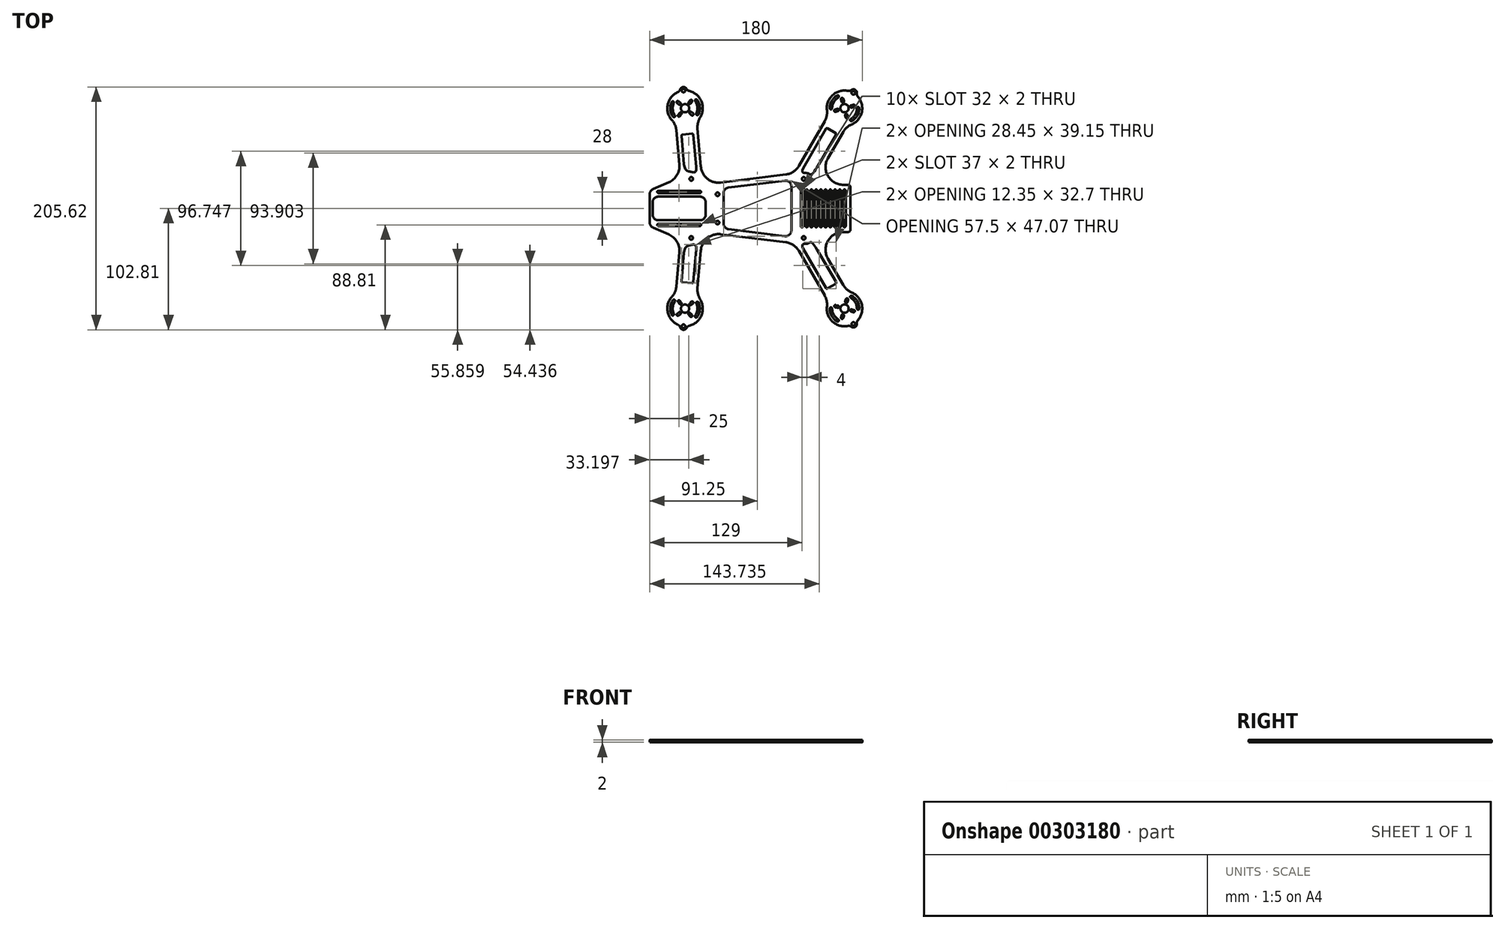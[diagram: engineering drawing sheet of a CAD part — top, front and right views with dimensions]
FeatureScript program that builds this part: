
annotation { "Feature Type Name" : "Feature", "Feature Type Description" : "" }
export const myFeature = defineFeature(function(context is Context, id is Id, definition is map)
    precondition{}
    {
        {
            var Q0;
            Q0=qCreatedBy(makeId("Top.planeOp"),FACE);
            var sketch = newSketch(context, id + "F0", { "sketchPlane" : qUnion([Q0])});
            skLineSegment(sketch, "E0", {"start": v(-85, 0) * mm, "end": v(85, 0) * mm, "construction": true});
            skLineSegment(sketch, "E1", {"start": v(-47.57, 0) * mm, "end": v(-55, -84.87) * mm, "construction": true});
            skLineSegment(sketch, "E2", {"start": v(31, 0) * mm, "end": v(80, -84.87) * mm, "construction": true});
            skArc(sketch, "E3", {"start": v(-66.17, -74.86) * mm, "mid": v(-69.65, -88.1) * mm, "end": v(-60.9, -98.66) * mm});
            skArc(sketch, "E4", {"start": v(65.1, -83.08) * mm, "mid": v(69.86, -95.92) * mm, "end": v(83.07, -99.55) * mm});
            skCircle(sketch, "E5", {"center": v(-55, -84.87) * mm, "radius": 3.5 * mm});
            skCircle(sketch, "E6", {"center": v(-55, -84.87) * mm, "radius": 6 * mm, "construction": true});
            skCircle(sketch, "E7", {"center": v(-55, -84.87) * mm, "radius": 8 * mm, "construction": true});
            skCircle(sketch, "E8", {"center": v(80, -84.87) * mm, "radius": 6 * mm, "construction": true});
            skCircle(sketch, "E9", {"center": v(80, -84.87) * mm, "radius": 8 * mm, "construction": true});
            skCircle(sketch, "E10", {"center": v(80, -84.87) * mm, "radius": 3.5 * mm});
            skLineSegment(sketch, "E11", {"start": v(-55, -84.87) * mm, "end": v(-58.86, -80.27) * mm, "construction": true});
            skLineSegment(sketch, "E12", {"start": v(80, -84.87) * mm, "end": v(81.55, -79.07) * mm, "construction": true});
            skLineSegment(sketch, "E13", {"start": v(-60.14, -78.74) * mm, "end": v(-64.05, -74.08) * mm, "construction": true});
            skLineSegment(sketch, "E14", {"start": v(-58.86, -80.27) * mm, "end": v(-60.14, -78.74) * mm, "construction": true});
            skArc(sketch, "E15.0.startCap", {"start": v(-58.1, -79.63) * mm, "mid": v(-58.21, -81.04) * mm, "end": v(-59.62, -80.92) * mm});
            skArc(sketch, "E15.0.endCap", {"start": v(-60.9, -79.38) * mm, "mid": v(-60.79, -77.98) * mm, "end": v(-59.38, -78.1) * mm});
            skLineSegment(sketch, "E15.0.left", {"start": v(-59.62, -80.92) * mm, "end": v(-60.9, -79.38) * mm});
            skLineSegment(sketch, "E15.0.right", {"start": v(-58.1, -79.63) * mm, "end": v(-59.38, -78.1) * mm});
            skArc(sketch, "E16.1.0", {"start": v(-60.49, -90.78) * mm, "mid": v(-61.9, -90.66) * mm, "end": v(-61.77, -89.25) * mm});
            skLineSegment(sketch, "E16.1.1", {"start": v(-60.24, -87.96) * mm, "end": v(-61.77, -89.25) * mm});
            skArc(sketch, "E16.1.2", {"start": v(-60.24, -87.96) * mm, "mid": v(-58.83, -88.08) * mm, "end": v(-58.95, -89.5) * mm});
            skLineSegment(sketch, "E16.1.3", {"start": v(-58.95, -89.5) * mm, "end": v(-60.49, -90.78) * mm});
            skArc(sketch, "E16.2.0", {"start": v(-49.1, -90.36) * mm, "mid": v(-49.21, -91.76) * mm, "end": v(-50.62, -91.64) * mm});
            skLineSegment(sketch, "E16.2.1", {"start": v(-51.9, -90.1) * mm, "end": v(-50.62, -91.64) * mm});
            skArc(sketch, "E16.2.2", {"start": v(-51.9, -90.1) * mm, "mid": v(-51.79, -88.7) * mm, "end": v(-50.38, -88.82) * mm});
            skLineSegment(sketch, "E16.2.3", {"start": v(-50.38, -88.82) * mm, "end": v(-49.1, -90.36) * mm});
            skArc(sketch, "E16.3.0", {"start": v(-49.51, -78.96) * mm, "mid": v(-48.1, -79.09) * mm, "end": v(-48.23, -80.5) * mm});
            skLineSegment(sketch, "E16.3.1", {"start": v(-49.76, -81.78) * mm, "end": v(-48.23, -80.5) * mm});
            skArc(sketch, "E16.3.2", {"start": v(-49.76, -81.78) * mm, "mid": v(-51.17, -81.66) * mm, "end": v(-51.05, -80.25) * mm});
            skLineSegment(sketch, "E16.3.3", {"start": v(-51.05, -80.25) * mm, "end": v(-49.51, -78.96) * mm});
            skCircle(sketch, "E17", {"center": v(-55, -84.87) * mm, "radius": 63.5 * mm, "construction": true});
            skCircle(sketch, "E18", {"center": v(80, -84.87) * mm, "radius": 63.5 * mm, "construction": true});
            skLineSegment(sketch, "E19", {"start": v(81.55, -79.07) * mm, "end": v(82.07, -77.14) * mm, "construction": true});
            skLineSegment(sketch, "E20", {"start": v(82.07, -77.14) * mm, "end": v(83.42, -72.1) * mm, "construction": true});
            skArc(sketch, "E21.0.startCap", {"start": v(82.52, -79.33) * mm, "mid": v(81.3, -80.04) * mm, "end": v(80.59, -78.82) * mm});
            skArc(sketch, "E21.0.endCap", {"start": v(81.1, -76.88) * mm, "mid": v(82.33, -76.18) * mm, "end": v(83.04, -77.4) * mm});
            skLineSegment(sketch, "E21.0.left", {"start": v(80.59, -78.82) * mm, "end": v(81.1, -76.88) * mm});
            skLineSegment(sketch, "E21.0.right", {"start": v(82.52, -79.33) * mm, "end": v(83.04, -77.4) * mm});
            skArc(sketch, "E22.1.0", {"start": v(72.01, -83.77) * mm, "mid": v(71.3, -82.54) * mm, "end": v(72.53, -81.83) * mm});
            skLineSegment(sketch, "E22.1.1", {"start": v(74.46, -82.35) * mm, "end": v(72.53, -81.83) * mm});
            skArc(sketch, "E22.1.2", {"start": v(74.46, -82.35) * mm, "mid": v(75.17, -83.58) * mm, "end": v(73.95, -84.28) * mm});
            skLineSegment(sketch, "E22.1.3", {"start": v(73.95, -84.28) * mm, "end": v(72.01, -83.77) * mm});
            skArc(sketch, "E22.2.0", {"start": v(78.9, -92.86) * mm, "mid": v(77.67, -93.56) * mm, "end": v(76.96, -92.34) * mm});
            skLineSegment(sketch, "E22.2.1", {"start": v(77.48, -90.4) * mm, "end": v(76.96, -92.34) * mm});
            skArc(sketch, "E22.2.2", {"start": v(77.48, -90.4) * mm, "mid": v(78.7, -89.7) * mm, "end": v(79.41, -90.92) * mm});
            skLineSegment(sketch, "E22.2.3", {"start": v(79.41, -90.92) * mm, "end": v(78.9, -92.86) * mm});
            skArc(sketch, "E22.3.0", {"start": v(87.99, -85.98) * mm, "mid": v(88.7, -87.2) * mm, "end": v(87.47, -87.9) * mm});
            skLineSegment(sketch, "E22.3.1", {"start": v(85.54, -87.39) * mm, "end": v(87.47, -87.9) * mm});
            skArc(sketch, "E22.3.2", {"start": v(85.54, -87.39) * mm, "mid": v(84.83, -86.16) * mm, "end": v(86.05, -85.46) * mm});
            skLineSegment(sketch, "E22.3.3", {"start": v(86.05, -85.46) * mm, "end": v(87.99, -85.98) * mm});
            skLineSegment(sketch, "E23", {"start": v(-85, 0) * mm, "end": v(-85, -11.72) * mm});
            skLineSegment(sketch, "E24", {"start": v(-59.85, -37.08) * mm, "end": v(-62.4, -66.15) * mm});
            skLineSegment(sketch, "E25", {"start": v(-44.47, -67.72) * mm, "end": v(-41.64, -35.47) * mm});
            skLineSegment(sketch, "E26", {"start": v(-24.87, -21.9) * mm, "end": v(30.26, -28.66) * mm});
            skLineSegment(sketch, "E27", {"start": v(41.42, -36.05) * mm, "end": v(63.2, -73.78) * mm});
            skLineSegment(sketch, "E28", {"start": v(78.8, -64.78) * mm, "end": v(65.93, -42.5) * mm});
            skLineSegment(sketch, "E29", {"start": v(78.92, -20) * mm, "end": v(83, -20) * mm});
            skLineSegment(sketch, "E30", {"start": v(85, -18) * mm, "end": v(85, 0) * mm});
            skPoint(sketch, "E31.visualSharp", {"position": v(-40.3, -20) * mm});
            skArc(sketch, "E31.filletArc", {"start": v(-24.87, -21.9) * mm, "mid": v(-36.14, -25.12) * mm, "end": v(-41.64, -35.47) * mm});
            skPoint(sketch, "E32.visualSharp", {"position": v(52.94, -20) * mm});
            skPoint(sketch, "E33.visualSharp", {"position": v(37.68, -29.57) * mm});
            skArc(sketch, "E33.filletArc", {"start": v(41.42, -36.05) * mm, "mid": v(36.71, -31.04) * mm, "end": v(30.26, -28.66) * mm});
            skPoint(sketch, "E34.visualSharp", {"position": v(85, -20) * mm});
            skArc(sketch, "E34.filletArc", {"start": v(83, -20) * mm, "mid": v(84.41, -19.41) * mm, "end": v(85, -18) * mm});
            skArc(sketch, "E35.filletArc", {"start": v(78.92, -20) * mm, "mid": v(65.93, -27.5) * mm, "end": v(65.93, -42.5) * mm});
            skPoint(sketch, "E36.visualSharp", {"position": v(-62.92, -72.13) * mm});
            skArc(sketch, "E36.filletArc", {"start": v(-66.17, -74.86) * mm, "mid": v(-63.58, -70.81) * mm, "end": v(-62.4, -66.15) * mm});
            skPoint(sketch, "E37.visualSharp", {"position": v(-44.99, -73.7) * mm});
            skArc(sketch, "E37.filletArc", {"start": v(-44.47, -67.72) * mm, "mid": v(-44.11, -72.52) * mm, "end": v(-42.26, -76.95) * mm});
            skPoint(sketch, "E38.visualSharp", {"position": v(66.2, -78.98) * mm});
            skArc(sketch, "E38.filletArc", {"start": v(65.1, -83.08) * mm, "mid": v(64.91, -78.27) * mm, "end": v(63.2, -73.78) * mm});
            skPoint(sketch, "E39.visualSharp", {"position": v(81.8, -69.98) * mm});
            skArc(sketch, "E39.filletArc", {"start": v(78.8, -64.78) * mm, "mid": v(81.83, -68.5) * mm, "end": v(85.9, -71.08) * mm});
            skLineSegment(sketch, "E40", {"start": v(-81.99, -16.3) * mm, "end": v(-68.83, -22) * mm});
            skPoint(sketch, "E41.visualSharp", {"position": v(-85, -15) * mm});
            skArc(sketch, "E41.filletArc", {"start": v(-85, -11.72) * mm, "mid": v(-84.18, -14.46) * mm, "end": v(-81.99, -16.3) * mm});
            skPoint(sketch, "E42.visualSharp", {"position": v(-58.91, -26.3) * mm});
            skArc(sketch, "E43.filletArc", {"start": v(-59.85, -37.08) * mm, "mid": v(-61.9, -28.1) * mm, "end": v(-68.83, -22) * mm});
            skLineSegment(sketch, "E44", {"start": v(78.92, -20) * mm, "end": v(-122.08, -20) * mm, "construction": true});
            skLineSegment(sketch, "E45", {"start": v(-55, -84.87) * mm, "end": v(80, -84.87) * mm, "construction": true});
            skLineSegment(sketch, "E46", {"start": v(-55, -84.87) * mm, "end": v(-57.29, -111.02) * mm, "construction": true});
            skLineSegment(sketch, "E47", {"start": v(80, -84.87) * mm, "end": v(94.45, -109.9) * mm, "construction": true});
            skArc(sketch, "E48.trimOffspring", {"start": v(-51.58, -99.47) * mm, "mid": v(-41.14, -90.6) * mm, "end": v(-42.26, -76.95) * mm});
            skCircle(sketch, "E49", {"center": v(87.5, -97.86) * mm, "radius": 1.5 * mm});
            skArc(sketch, "E50", {"start": v(85.6, -100.18) * mm, "mid": v(89, -100.46) * mm, "end": v(90.46, -97.37) * mm});
            skArc(sketch, "E51.trimOffspring", {"start": v(91.18, -94.87) * mm, "mid": v(94.64, -81.62) * mm, "end": v(85.9, -71.08) * mm});
            skPoint(sketch, "E52.visualSharp", {"position": v(89.94, -96.1) * mm});
            skArc(sketch, "E52.filletArc", {"start": v(91.18, -94.87) * mm, "mid": v(90.54, -96.04) * mm, "end": v(90.46, -97.37) * mm});
            skPoint(sketch, "E53.visualSharp", {"position": v(84.76, -99.1) * mm});
            skArc(sketch, "E54.filletArc", {"start": v(85.6, -100.18) * mm, "mid": v(84.4, -99.58) * mm, "end": v(83.07, -99.55) * mm});
            skCircle(sketch, "E55", {"center": v(-49.76, -25) * mm, "radius": 1.5 * mm});
            skCircle(sketch, "E56", {"center": v(45.43, -25) * mm, "radius": 1.5 * mm});
            skCircle(sketch, "E57", {"center": v(-56.3, -99.81) * mm, "radius": 1.5 * mm});
            skArc(sketch, "E58", {"start": v(-59.2, -100.61) * mm, "mid": v(-56.57, -102.8) * mm, "end": v(-53.6, -101.1) * mm});
            skPoint(sketch, "E59.visualSharp", {"position": v(-53.3, -99.77) * mm});
            skArc(sketch, "E59.filletArc", {"start": v(-51.58, -99.47) * mm, "mid": v(-52.77, -100.06) * mm, "end": v(-53.6, -101.1) * mm});
            skPoint(sketch, "E60.visualSharp", {"position": v(-59.25, -99.25) * mm});
            skArc(sketch, "E60.filletArc", {"start": v(-59.2, -100.61) * mm, "mid": v(-59.83, -99.44) * mm, "end": v(-60.9, -98.66) * mm});
            skLineSegment(sketch, "E61.MirrorCS", {"start": v(81.55, 79.07) * mm, "end": v(82.07, 77.14) * mm, "construction": true});
            skLineSegment(sketch, "E62.MirrorCS", {"start": v(80.59, 78.82) * mm, "end": v(81.1, 76.88) * mm});
            skLineSegment(sketch, "E63.MirrorCS", {"start": v(82.52, 79.33) * mm, "end": v(83.04, 77.4) * mm});
            skArc(sketch, "E64.MirrorCS", {"start": v(81.1, 76.88) * mm, "mid": v(82.33, 76.18) * mm, "end": v(83.04, 77.4) * mm});
            skLineSegment(sketch, "E65.MirrorCS", {"start": v(-55, 84.87) * mm, "end": v(-58.86, 80.27) * mm, "construction": true});
            skLineSegment(sketch, "E66.MirrorCS", {"start": v(78.92, 20) * mm, "end": v(83, 20) * mm});
            skCircle(sketch, "E67.MirrorC", {"center": v(-56.3, 99.81) * mm, "radius": 1.5 * mm});
            skLineSegment(sketch, "E68.MirrorCS", {"start": v(-58.86, 80.27) * mm, "end": v(-60.14, 78.74) * mm, "construction": true});
            skArc(sketch, "E69.MirrorCS", {"start": v(-58.1, 79.63) * mm, "mid": v(-58.21, 81.04) * mm, "end": v(-59.62, 80.92) * mm});
            skLineSegment(sketch, "E70.MirrorCS", {"start": v(-59.62, 80.92) * mm, "end": v(-60.9, 79.38) * mm});
            skLineSegment(sketch, "E71.MirrorCS", {"start": v(-58.1, 79.63) * mm, "end": v(-59.38, 78.1) * mm});
            skArc(sketch, "E72.MirrorCS", {"start": v(82.52, 79.33) * mm, "mid": v(81.3, 80.04) * mm, "end": v(80.59, 78.82) * mm});
            skArc(sketch, "E73.MirrorCS", {"start": v(-60.9, 79.38) * mm, "mid": v(-60.79, 77.98) * mm, "end": v(-59.38, 78.1) * mm});
            skCircle(sketch, "E74.MirrorC", {"center": v(87.5, 97.86) * mm, "radius": 1.5 * mm});
            skLineSegment(sketch, "E75.MirrorCS", {"start": v(-58.95, 89.5) * mm, "end": v(-60.49, 90.78) * mm});
            skLineSegment(sketch, "E76.MirrorCS", {"start": v(85.54, 87.39) * mm, "end": v(87.47, 87.9) * mm});
            skArc(sketch, "E77.MirrorCS", {"start": v(-60.49, 90.78) * mm, "mid": v(-61.9, 90.66) * mm, "end": v(-61.77, 89.25) * mm});
            skArc(sketch, "E78.MirrorCS", {"start": v(91.18, 94.87) * mm, "mid": v(90.54, 96.04) * mm, "end": v(90.46, 97.37) * mm});
            skArc(sketch, "E79.MirrorCS", {"start": v(72.01, 83.77) * mm, "mid": v(71.3, 82.54) * mm, "end": v(72.53, 81.83) * mm});
            skArc(sketch, "E80.MirrorCS", {"start": v(74.46, 82.35) * mm, "mid": v(75.17, 83.58) * mm, "end": v(73.95, 84.28) * mm});
            skLineSegment(sketch, "E81.MirrorCS", {"start": v(-60.24, 87.96) * mm, "end": v(-61.77, 89.25) * mm});
            skLineSegment(sketch, "E82.MirrorCS", {"start": v(77.48, 90.4) * mm, "end": v(76.96, 92.34) * mm});
            skLineSegment(sketch, "E83.MirrorCS", {"start": v(-51.9, 90.1) * mm, "end": v(-50.62, 91.64) * mm});
            skArc(sketch, "E84.MirrorCS", {"start": v(85.54, 87.39) * mm, "mid": v(84.83, 86.16) * mm, "end": v(86.05, 85.46) * mm});
            skArc(sketch, "E85.MirrorCS", {"start": v(-51.9, 90.1) * mm, "mid": v(-51.79, 88.7) * mm, "end": v(-50.38, 88.82) * mm});
            skArc(sketch, "E86.MirrorCS", {"start": v(-49.76, 81.78) * mm, "mid": v(-51.17, 81.66) * mm, "end": v(-51.05, 80.25) * mm});
            skLineSegment(sketch, "E87.MirrorCS", {"start": v(-51.05, 80.25) * mm, "end": v(-49.51, 78.96) * mm});
            skLineSegment(sketch, "E88.MirrorCS", {"start": v(79.41, 90.92) * mm, "end": v(78.9, 92.86) * mm});
            skLineSegment(sketch, "E89.MirrorCS", {"start": v(-50.38, 88.82) * mm, "end": v(-49.1, 90.36) * mm});
            skArc(sketch, "E90.MirrorCS", {"start": v(85.6, 100.18) * mm, "mid": v(84.4, 99.58) * mm, "end": v(83.07, 99.55) * mm});
            skLineSegment(sketch, "E91.MirrorCS", {"start": v(-49.76, 81.78) * mm, "end": v(-48.23, 80.5) * mm});
            skLineSegment(sketch, "E92.MirrorCS", {"start": v(74.46, 82.35) * mm, "end": v(72.53, 81.83) * mm});
            skArc(sketch, "E93.MirrorCS", {"start": v(-49.1, 90.36) * mm, "mid": v(-49.21, 91.76) * mm, "end": v(-50.62, 91.64) * mm});
            skArc(sketch, "E94.MirrorCS", {"start": v(-60.24, 87.96) * mm, "mid": v(-58.83, 88.08) * mm, "end": v(-58.95, 89.5) * mm});
            skArc(sketch, "E95.MirrorCS", {"start": v(-49.51, 78.96) * mm, "mid": v(-48.1, 79.09) * mm, "end": v(-48.23, 80.5) * mm});
            skArc(sketch, "E96.MirrorCS", {"start": v(78.9, 92.86) * mm, "mid": v(77.67, 93.56) * mm, "end": v(76.96, 92.34) * mm});
            skLineSegment(sketch, "E97.MirrorCS", {"start": v(86.05, 85.46) * mm, "end": v(87.99, 85.98) * mm});
            skArc(sketch, "E98.MirrorCS", {"start": v(87.99, 85.98) * mm, "mid": v(88.7, 87.2) * mm, "end": v(87.47, 87.9) * mm});
            skArc(sketch, "E99.MirrorCS", {"start": v(77.48, 90.4) * mm, "mid": v(78.7, 89.7) * mm, "end": v(79.41, 90.92) * mm});
            skLineSegment(sketch, "E100.MirrorCS", {"start": v(73.95, 84.28) * mm, "end": v(72.01, 83.77) * mm});
            skCircle(sketch, "E101.MirrorC", {"center": v(45.43, 25) * mm, "radius": 1.5 * mm});
            skCircle(sketch, "E102.MirrorC", {"center": v(80, 84.87) * mm, "radius": 3.5 * mm});
            skArc(sketch, "E103.MirrorCS", {"start": v(78.8, 64.78) * mm, "mid": v(81.83, 68.5) * mm, "end": v(85.9, 71.08) * mm});
            skCircle(sketch, "E104.MirrorC", {"center": v(-49.76, 25) * mm, "radius": 1.5 * mm});
            skPoint(sketch, "E105.MirrorP", {"position": v(52.94, 20) * mm});
            skPoint(sketch, "E106.MirrorP", {"position": v(-58.91, 26.3) * mm});
            skArc(sketch, "E107.MirrorCS", {"start": v(65.1, 83.08) * mm, "mid": v(64.91, 78.27) * mm, "end": v(63.2, 73.78) * mm});
            skLineSegment(sketch, "E108.MirrorCS", {"start": v(-55, 84.87) * mm, "end": v(-57.29, 111.02) * mm, "construction": true});
            skArc(sketch, "E109.MirrorCS", {"start": v(83, 20) * mm, "mid": v(84.41, 19.41) * mm, "end": v(85, 18) * mm});
            skLineSegment(sketch, "E110.MirrorCS", {"start": v(82.07, 77.14) * mm, "end": v(83.42, 72.1) * mm, "construction": true});
            skPoint(sketch, "E111.MirrorP", {"position": v(84.76, 99.1) * mm});
            skCircle(sketch, "E112.MirrorC", {"center": v(-55, 84.87) * mm, "radius": 3.5 * mm});
            skLineSegment(sketch, "E113.MirrorCS", {"start": v(-60.14, 78.74) * mm, "end": v(-64.05, 74.08) * mm, "construction": true});
            skLineSegment(sketch, "E114.MirrorCS", {"start": v(80, 84.87) * mm, "end": v(81.55, 79.07) * mm, "construction": true});
            skLineSegment(sketch, "E115.MirrorCS", {"start": v(78.92, 20) * mm, "end": v(-122.08, 20) * mm, "construction": true});
            skPoint(sketch, "E116.MirrorP", {"position": v(85, 20) * mm});
            skPoint(sketch, "E117.MirrorP", {"position": v(-62.92, 72.13) * mm});
            skArc(sketch, "E118.MirrorCS", {"start": v(-51.58, 99.47) * mm, "mid": v(-41.14, 90.6) * mm, "end": v(-42.26, 76.95) * mm});
            skCircle(sketch, "E119.MirrorC", {"center": v(-55, 84.87) * mm, "radius": 8 * mm, "construction": true});
            skLineSegment(sketch, "E120.MirrorCS", {"start": v(85, 18) * mm, "end": v(85, 0) * mm});
            skArc(sketch, "E121.MirrorCS", {"start": v(-59.85, 37.08) * mm, "mid": v(-61.9, 28.1) * mm, "end": v(-68.83, 22) * mm});
            skLineSegment(sketch, "E122.MirrorCS", {"start": v(-47.57, 0) * mm, "end": v(-55, 84.87) * mm, "construction": true});
            skArc(sketch, "E123.MirrorCS", {"start": v(-85, 11.72) * mm, "mid": v(-84.18, 14.46) * mm, "end": v(-81.99, 16.3) * mm});
            skLineSegment(sketch, "E124.MirrorCS", {"start": v(-44.47, 67.72) * mm, "end": v(-41.64, 35.47) * mm});
            skCircle(sketch, "E125.MirrorC", {"center": v(-55, 84.87) * mm, "radius": 6 * mm, "construction": true});
            skLineSegment(sketch, "E126.MirrorCS", {"start": v(41.42, 36.05) * mm, "end": v(63.2, 73.78) * mm});
            skLineSegment(sketch, "E127.MirrorCS", {"start": v(80, 84.87) * mm, "end": v(94.45, 109.9) * mm, "construction": true});
            skLineSegment(sketch, "E128.MirrorCS", {"start": v(78.8, 64.78) * mm, "end": v(65.93, 42.5) * mm});
            skPoint(sketch, "E129.MirrorP", {"position": v(-53.3, 99.77) * mm});
            skLineSegment(sketch, "E130.MirrorCS", {"start": v(-24.87, 21.9) * mm, "end": v(30.26, 28.66) * mm});
            skPoint(sketch, "E131.MirrorP", {"position": v(-44.99, 73.7) * mm});
            skArc(sketch, "E132.MirrorCS", {"start": v(-66.17, 74.86) * mm, "mid": v(-63.58, 70.81) * mm, "end": v(-62.4, 66.15) * mm});
            skArc(sketch, "E133.MirrorCS", {"start": v(78.92, 20) * mm, "mid": v(65.93, 27.5) * mm, "end": v(65.93, 42.5) * mm});
            skPoint(sketch, "E134.MirrorP", {"position": v(-59.25, 99.25) * mm});
            skArc(sketch, "E135.MirrorCS", {"start": v(41.42, 36.05) * mm, "mid": v(36.71, 31.04) * mm, "end": v(30.26, 28.66) * mm});
            skLineSegment(sketch, "E136.MirrorCS", {"start": v(-85, 0) * mm, "end": v(-85, 11.72) * mm});
            skPoint(sketch, "E137.MirrorP", {"position": v(37.68, 29.57) * mm});
            skPoint(sketch, "E138.MirrorP", {"position": v(81.8, 69.98) * mm});
            skArc(sketch, "E139.MirrorCS", {"start": v(-44.47, 67.72) * mm, "mid": v(-44.11, 72.52) * mm, "end": v(-42.26, 76.95) * mm});
            skCircle(sketch, "E140.MirrorC", {"center": v(-55, 84.87) * mm, "radius": 63.5 * mm, "construction": true});
            skCircle(sketch, "E141.MirrorC", {"center": v(80, 84.87) * mm, "radius": 63.5 * mm, "construction": true});
            skPoint(sketch, "E142.MirrorP", {"position": v(66.2, 78.98) * mm});
            skLineSegment(sketch, "E143.MirrorCS", {"start": v(-55, 84.87) * mm, "end": v(80, 84.87) * mm, "construction": true});
            skPoint(sketch, "E144.MirrorP", {"position": v(-40.3, 20) * mm});
            skLineSegment(sketch, "E145.MirrorCS", {"start": v(-59.85, 37.08) * mm, "end": v(-62.4, 66.15) * mm});
            skCircle(sketch, "E146.MirrorC", {"center": v(80, 84.87) * mm, "radius": 8 * mm, "construction": true});
            skArc(sketch, "E147.MirrorCS", {"start": v(85.6, 100.18) * mm, "mid": v(89, 100.46) * mm, "end": v(90.46, 97.37) * mm});
            skArc(sketch, "E148.MirrorCS", {"start": v(-59.2, 100.61) * mm, "mid": v(-56.57, 102.8) * mm, "end": v(-53.6, 101.1) * mm});
            skCircle(sketch, "E149.MirrorC", {"center": v(80, 84.87) * mm, "radius": 6 * mm, "construction": true});
            skLineSegment(sketch, "E150.MirrorCS", {"start": v(31, 0) * mm, "end": v(80, 84.87) * mm, "construction": true});
            skPoint(sketch, "E151.MirrorP", {"position": v(89.94, 96.1) * mm});
            skPoint(sketch, "E152.MirrorP", {"position": v(-85, 15) * mm});
            skArc(sketch, "E153.MirrorCS", {"start": v(91.18, 94.87) * mm, "mid": v(94.64, 81.62) * mm, "end": v(85.9, 71.08) * mm});
            skArc(sketch, "E154.MirrorCS", {"start": v(65.1, 83.08) * mm, "mid": v(69.86, 95.92) * mm, "end": v(83.07, 99.55) * mm});
            skArc(sketch, "E155.MirrorCS", {"start": v(-66.17, 74.86) * mm, "mid": v(-69.65, 88.1) * mm, "end": v(-60.9, 98.66) * mm});
            skArc(sketch, "E156.MirrorCS", {"start": v(-24.87, 21.9) * mm, "mid": v(-36.14, 25.12) * mm, "end": v(-41.64, 35.47) * mm});
            skLineSegment(sketch, "E157.MirrorCS", {"start": v(-81.99, 16.3) * mm, "end": v(-68.83, 22) * mm});
            skArc(sketch, "E158.filletArc", {"start": v(-60.9, 98.66) * mm, "mid": v(-59.83, 99.44) * mm, "end": v(-59.2, 100.61) * mm});
            skArc(sketch, "E159.filletArc", {"start": v(-53.6, 101.1) * mm, "mid": v(-52.77, 100.06) * mm, "end": v(-51.58, 99.47) * mm});
            skLineSegment(sketch, "E160.bottom", {"start": v(-42.5, -10) * mm, "end": v(-77.5, -10) * mm});
            skLineSegment(sketch, "E160.top", {"start": v(-42.5, 10) * mm, "end": v(-77.5, 10) * mm});
            skLineSegment(sketch, "E160.left", {"start": v(-37.5, -5) * mm, "end": v(-37.5, 5) * mm});
            skLineSegment(sketch, "E160.right", {"start": v(-82.5, -5) * mm, "end": v(-82.5, 5) * mm});
            skPoint(sketch, "E160.middle", {"position": v(-60, 0) * mm});
            skPoint(sketch, "E161.visualSharp", {"position": v(-37.5, 10) * mm});
            skArc(sketch, "E161.filletArc", {"start": v(-37.5, 5) * mm, "mid": v(-38.96, 8.54) * mm, "end": v(-42.5, 10) * mm});
            skPoint(sketch, "E162.visualSharp", {"position": v(-82.5, -10) * mm});
            skArc(sketch, "E162.filletArc", {"start": v(-82.5, -5) * mm, "mid": v(-81.04, -8.54) * mm, "end": v(-77.5, -10) * mm});
            skPoint(sketch, "E163.visualSharp", {"position": v(-82.5, 10) * mm});
            skArc(sketch, "E163.filletArc", {"start": v(-77.5, 10) * mm, "mid": v(-81.04, 8.54) * mm, "end": v(-82.5, 5) * mm});
            skPoint(sketch, "E164.visualSharp", {"position": v(-37.5, -10) * mm});
            skArc(sketch, "E164.filletArc", {"start": v(-42.5, -10) * mm, "mid": v(-38.96, -8.54) * mm, "end": v(-37.5, -5) * mm});
            skLineSegment(sketch, "E165.3", {"start": v(72.83, -62.45) * mm, "end": v(62.47, -44.5) * mm});
            skLineSegment(sketch, "E165.11", {"start": v(-55.87, -37.43) * mm, "end": v(-57.98, -61.52) * mm});
            skLineSegment(sketch, "E165.18", {"start": v(-48.01, -62.4) * mm, "end": v(-45.63, -35.13) * mm});
            skLineSegment(sketch, "E165.20", {"start": v(-18.1, -17.69) * mm, "end": v(29.4, -23.52) * mm});
            skLineSegment(sketch, "E165.22", {"start": v(44.89, -34.05) * mm, "end": v(64.17, -67.45) * mm});
            skLineSegment(sketch, "E166", {"start": v(-57.07, -62.6) * mm, "end": v(-49.1, -63.3) * mm});
            skLineSegment(sketch, "E167", {"start": v(65.54, -67.82) * mm, "end": v(72.46, -63.82) * mm});
            skFitSpline(sketch, "E168", {"points": [v(-55.87, -37.43) * mm, v(-50.29, -31) * mm, v(-45.63, -35.13) * mm], "startDerivative": vector(4.25, 32.5) * mm, "endDerivative": vector(-4.16, -37.68) * mm});
            skFitSpline(sketch, "E169", {"points": [v(62.47, -44.5) * mm, v(48.25, -29.88) * mm, v(44.89, -34.05) * mm], "startDerivative": vector(-54.1, 94.98) * mm, "endDerivative": vector(18.1, -43.24) * mm});
            skLineSegment(sketch, "E170", {"start": v(-22.5, -12.72) * mm, "end": v(-22.5, 0) * mm});
            skLineSegment(sketch, "E171", {"start": v(35, -18.56) * mm, "end": v(35, 0) * mm});
            skPoint(sketch, "E172.visualSharp", {"position": v(-22.5, -17.15) * mm});
            skArc(sketch, "E172.filletArc", {"start": v(-22.5, -12.72) * mm, "mid": v(-21.24, -16.04) * mm, "end": v(-18.1, -17.69) * mm});
            skPoint(sketch, "E173.visualSharp", {"position": v(35, -24.2) * mm});
            skArc(sketch, "E173.filletArc", {"start": v(29.4, -23.52) * mm, "mid": v(33.31, -22.3) * mm, "end": v(35, -18.56) * mm});
            skPoint(sketch, "E174.visualSharp", {"position": v(-58.06, -62.52) * mm});
            skArc(sketch, "E174.filletArc", {"start": v(-57.98, -61.52) * mm, "mid": v(-57.75, -62.25) * mm, "end": v(-57.07, -62.6) * mm});
            skPoint(sketch, "E175.visualSharp", {"position": v(-48.1, -63.39) * mm});
            skArc(sketch, "E175.filletArc", {"start": v(-49.1, -63.3) * mm, "mid": v(-48.37, -63.07) * mm, "end": v(-48.01, -62.4) * mm});
            skPoint(sketch, "E176.visualSharp", {"position": v(64.67, -68.32) * mm});
            skArc(sketch, "E176.filletArc", {"start": v(64.17, -67.45) * mm, "mid": v(64.78, -67.92) * mm, "end": v(65.54, -67.82) * mm});
            skPoint(sketch, "E177.visualSharp", {"position": v(73.33, -63.32) * mm});
            skArc(sketch, "E177.filletArc", {"start": v(72.46, -63.82) * mm, "mid": v(72.93, -63.21) * mm, "end": v(72.83, -62.45) * mm});
            skLineSegment(sketch, "E178", {"start": v(80, 15) * mm, "end": v(80, -15) * mm, "construction": true});
            skArc(sketch, "E179.0.startCap", {"start": v(79, 15) * mm, "mid": v(80, 16) * mm, "end": v(81, 15) * mm});
            skArc(sketch, "E179.0.endCap", {"start": v(81, -15) * mm, "mid": v(80, -16) * mm, "end": v(79, -15) * mm});
            skLineSegment(sketch, "E179.0.left", {"start": v(81, 15) * mm, "end": v(81, -15) * mm});
            skLineSegment(sketch, "E179.0.right", {"start": v(79, 15) * mm, "end": v(79, -15) * mm});
            skLineSegment(sketch, "E180.1.0.0", {"start": v(75, 15) * mm, "end": v(75, -15) * mm});
            skArc(sketch, "E180.1.0.1", {"start": v(77, -15) * mm, "mid": v(76, -16) * mm, "end": v(75, -15) * mm});
            skLineSegment(sketch, "E180.1.0.2", {"start": v(77, 15) * mm, "end": v(77, -15) * mm});
            skArc(sketch, "E180.1.0.3", {"start": v(75, 15) * mm, "mid": v(76, 16) * mm, "end": v(77, 15) * mm});
            skLineSegment(sketch, "E180.2.0.0", {"start": v(71, 15) * mm, "end": v(71, -15) * mm});
            skArc(sketch, "E180.2.0.1", {"start": v(73, -15) * mm, "mid": v(72, -16) * mm, "end": v(71, -15) * mm});
            skLineSegment(sketch, "E180.2.0.2", {"start": v(73, 15) * mm, "end": v(73, -15) * mm});
            skArc(sketch, "E180.2.0.3", {"start": v(71, 15) * mm, "mid": v(72, 16) * mm, "end": v(73, 15) * mm});
            skLineSegment(sketch, "E180.3.0.0", {"start": v(67, 15) * mm, "end": v(67, -15) * mm});
            skArc(sketch, "E180.3.0.1", {"start": v(69, -15) * mm, "mid": v(68, -16) * mm, "end": v(67, -15) * mm});
            skLineSegment(sketch, "E180.3.0.2", {"start": v(69, 15) * mm, "end": v(69, -15) * mm});
            skArc(sketch, "E180.3.0.3", {"start": v(67, 15) * mm, "mid": v(68, 16) * mm, "end": v(69, 15) * mm});
            skLineSegment(sketch, "E180.4.0.0", {"start": v(63, 15) * mm, "end": v(63, -15) * mm});
            skArc(sketch, "E180.4.0.1", {"start": v(65, -15) * mm, "mid": v(64, -16) * mm, "end": v(63, -15) * mm});
            skLineSegment(sketch, "E180.4.0.2", {"start": v(65, 15) * mm, "end": v(65, -15) * mm});
            skArc(sketch, "E180.4.0.3", {"start": v(63, 15) * mm, "mid": v(64, 16) * mm, "end": v(65, 15) * mm});
            skLineSegment(sketch, "E180.5.0.0", {"start": v(59, 15) * mm, "end": v(59, -15) * mm});
            skArc(sketch, "E180.5.0.1", {"start": v(61, -15) * mm, "mid": v(60, -16) * mm, "end": v(59, -15) * mm});
            skLineSegment(sketch, "E180.5.0.2", {"start": v(61, 15) * mm, "end": v(61, -15) * mm});
            skArc(sketch, "E180.5.0.3", {"start": v(59, 15) * mm, "mid": v(60, 16) * mm, "end": v(61, 15) * mm});
            skLineSegment(sketch, "E180.6.0.0", {"start": v(55, 15) * mm, "end": v(55, -15) * mm});
            skArc(sketch, "E180.6.0.1", {"start": v(57, -15) * mm, "mid": v(56, -16) * mm, "end": v(55, -15) * mm});
            skLineSegment(sketch, "E180.6.0.2", {"start": v(57, 15) * mm, "end": v(57, -15) * mm});
            skArc(sketch, "E180.6.0.3", {"start": v(55, 15) * mm, "mid": v(56, 16) * mm, "end": v(57, 15) * mm});
            skLineSegment(sketch, "E180.7.0.0", {"start": v(51, 15) * mm, "end": v(51, -15) * mm});
            skArc(sketch, "E180.7.0.1", {"start": v(53, -15) * mm, "mid": v(52, -16) * mm, "end": v(51, -15) * mm});
            skLineSegment(sketch, "E180.7.0.2", {"start": v(53, 15) * mm, "end": v(53, -15) * mm});
            skArc(sketch, "E180.7.0.3", {"start": v(51, 15) * mm, "mid": v(52, 16) * mm, "end": v(53, 15) * mm});
            skLineSegment(sketch, "E180.8.0.0", {"start": v(47, 15) * mm, "end": v(47, -15) * mm});
            skArc(sketch, "E180.8.0.1", {"start": v(49, -15) * mm, "mid": v(48, -16) * mm, "end": v(47, -15) * mm});
            skLineSegment(sketch, "E180.8.0.2", {"start": v(49, 15) * mm, "end": v(49, -15) * mm});
            skArc(sketch, "E180.8.0.3", {"start": v(47, 15) * mm, "mid": v(48, 16) * mm, "end": v(49, 15) * mm});
            skLineSegment(sketch, "E180.9.0.0", {"start": v(43, 15) * mm, "end": v(43, -15) * mm});
            skArc(sketch, "E180.9.0.1", {"start": v(45, -15) * mm, "mid": v(44, -16) * mm, "end": v(43, -15) * mm});
            skLineSegment(sketch, "E180.9.0.2", {"start": v(45, 15) * mm, "end": v(45, -15) * mm});
            skArc(sketch, "E180.9.0.3", {"start": v(43, 15) * mm, "mid": v(44, 16) * mm, "end": v(45, 15) * mm});
            skLineSegment(sketch, "E180.direction1", {"start": v(79, -15) * mm, "end": v(75, -15) * mm, "construction": true});
            skArc(sketch, "E181.MirrorCS", {"start": v(64.17, 67.45) * mm, "mid": v(64.78, 67.92) * mm, "end": v(65.54, 67.82) * mm});
            skArc(sketch, "E182.MirrorCS", {"start": v(72.46, 63.82) * mm, "mid": v(72.93, 63.21) * mm, "end": v(72.83, 62.45) * mm});
            skLineSegment(sketch, "E183.MirrorCS", {"start": v(65.54, 67.82) * mm, "end": v(72.46, 63.82) * mm});
            skLineSegment(sketch, "E184.MirrorCS", {"start": v(72.83, 62.45) * mm, "end": v(62.47, 44.5) * mm});
            skLineSegment(sketch, "E185.MirrorCS", {"start": v(44.89, 34.05) * mm, "end": v(64.17, 67.45) * mm});
            skFitSpline(sketch, "E186.MirrorCS", {"points": [v(62.47, 44.5) * mm, v(48.25, 29.88) * mm, v(44.89, 34.05) * mm], "startDerivative": vector(-54.1, -94.98) * mm, "endDerivative": vector(18.1, 43.24) * mm});
            skLineSegment(sketch, "E187.MirrorCS", {"start": v(35, 18.56) * mm, "end": v(35, 0) * mm});
            skArc(sketch, "E188.MirrorCS", {"start": v(29.4, 23.52) * mm, "mid": v(33.31, 22.3) * mm, "end": v(35, 18.56) * mm});
            skLineSegment(sketch, "E189.MirrorCS", {"start": v(-18.1, 17.69) * mm, "end": v(29.4, 23.52) * mm});
            skArc(sketch, "E190.MirrorCS", {"start": v(-22.5, 12.72) * mm, "mid": v(-21.24, 16.04) * mm, "end": v(-18.1, 17.69) * mm});
            skLineSegment(sketch, "E191.MirrorCS", {"start": v(-22.5, 12.72) * mm, "end": v(-22.5, 0) * mm});
            skLineSegment(sketch, "E192.MirrorCS", {"start": v(-48.01, 62.4) * mm, "end": v(-45.63, 35.13) * mm});
            skArc(sketch, "E193.MirrorCS", {"start": v(-49.1, 63.3) * mm, "mid": v(-48.37, 63.07) * mm, "end": v(-48.01, 62.4) * mm});
            skLineSegment(sketch, "E194.MirrorCS", {"start": v(-55.87, 37.43) * mm, "end": v(-57.98, 61.52) * mm});
            skLineSegment(sketch, "E195.MirrorCS", {"start": v(-57.07, 62.6) * mm, "end": v(-49.1, 63.3) * mm});
            skArc(sketch, "E196.MirrorCS", {"start": v(-57.98, 61.52) * mm, "mid": v(-57.75, 62.25) * mm, "end": v(-57.07, 62.6) * mm});
            skFitSpline(sketch, "E197.MirrorCS", {"points": [v(-55.87, 37.43) * mm, v(-50.29, 31) * mm, v(-45.63, 35.13) * mm], "startDerivative": vector(4.25, -32.5) * mm, "endDerivative": vector(-4.16, 37.68) * mm});
            skLineSegment(sketch, "E198.0", {"start": v(-42.5, -14) * mm, "end": v(-77.5, -14) * mm, "construction": true});
            skArc(sketch, "E199.0.startCap", {"start": v(-42.5, -13) * mm, "mid": v(-41.5, -14) * mm, "end": v(-42.5, -15) * mm});
            skArc(sketch, "E199.0.endCap", {"start": v(-77.5, -15) * mm, "mid": v(-78.5, -14) * mm, "end": v(-77.5, -13) * mm});
            skLineSegment(sketch, "E199.0.left", {"start": v(-42.5, -15) * mm, "end": v(-77.5, -15) * mm});
            skLineSegment(sketch, "E199.0.right", {"start": v(-42.5, -13) * mm, "end": v(-77.5, -13) * mm});
            skArc(sketch, "E200.MirrorCS", {"start": v(-42.5, 13) * mm, "mid": v(-41.5, 14) * mm, "end": v(-42.5, 15) * mm});
            skArc(sketch, "E201.MirrorCS", {"start": v(-77.5, 15) * mm, "mid": v(-78.5, 14) * mm, "end": v(-77.5, 13) * mm});
            skLineSegment(sketch, "E202.MirrorCS", {"start": v(-42.5, 15) * mm, "end": v(-77.5, 15) * mm});
            skLineSegment(sketch, "E203.MirrorCS", {"start": v(-42.5, 13) * mm, "end": v(-77.5, 13) * mm});
            skArc(sketch, "E204", {"start": v(-64.42, -78.27) * mm, "mid": v(-66.46, -83.87) * mm, "end": v(-65.42, -89.73) * mm, "construction": true});
            skLineSegment(sketch, "E205", {"start": v(-74.29, -93.86) * mm, "end": v(-55, -84.87) * mm, "construction": true});
            skLineSegment(sketch, "E206", {"start": v(-55, -84.87) * mm, "end": v(-37.16, -97.36) * mm, "construction": true});
            skLineSegment(sketch, "E207", {"start": v(-55, -84.87) * mm, "end": v(-37.47, -76.7) * mm, "construction": true});
            skLineSegment(sketch, "E208", {"start": v(-55, -84.87) * mm, "end": v(-69.19, -74.94) * mm, "construction": true});
            skArc(sketch, "E209.trimOffspring", {"start": v(-45.58, -91.47) * mm, "mid": v(-43.54, -85.87) * mm, "end": v(-44.58, -80.01) * mm, "construction": true});
            skArc(sketch, "E210.0.startCap", {"start": v(-65.24, -77.7) * mm, "mid": v(-63.85, -77.46) * mm, "end": v(-63.6, -78.85) * mm});
            skArc(sketch, "E210.0.endCap", {"start": v(-64.52, -89.3) * mm, "mid": v(-65, -90.64) * mm, "end": v(-66.33, -90.15) * mm});
            skArc(sketch, "E210.0.left", {"start": v(-63.6, -78.85) * mm, "mid": v(-65.46, -83.96) * mm, "end": v(-64.52, -89.3) * mm});
            skArc(sketch, "E210.0.right", {"start": v(-65.24, -77.7) * mm, "mid": v(-67.45, -83.78) * mm, "end": v(-66.33, -90.15) * mm});
            skArc(sketch, "E210.1.startCap", {"start": v(-44.76, -92.04) * mm, "mid": v(-46.15, -92.29) * mm, "end": v(-46.4, -90.9) * mm});
            skArc(sketch, "E210.1.endCap", {"start": v(-45.48, -80.43) * mm, "mid": v(-45, -79.1) * mm, "end": v(-43.67, -79.59) * mm});
            skArc(sketch, "E210.1.left", {"start": v(-46.4, -90.9) * mm, "mid": v(-44.54, -85.79) * mm, "end": v(-45.48, -80.43) * mm});
            skArc(sketch, "E210.1.right", {"start": v(-44.76, -92.04) * mm, "mid": v(-42.55, -85.96) * mm, "end": v(-43.67, -79.59) * mm});
            skLineSegment(sketch, "E211", {"start": v(80, -84.87) * mm, "end": v(56.08, -84.87) * mm, "construction": true});
            skLineSegment(sketch, "E212", {"start": v(80, -84.87) * mm, "end": v(70, -102.2) * mm, "construction": true});
            skLineSegment(sketch, "E213", {"start": v(80, -84.87) * mm, "end": v(89.28, -68.8) * mm, "construction": true});
            skLineSegment(sketch, "E214", {"start": v(80, -84.87) * mm, "end": v(100.14, -84.87) * mm, "construction": true});
            skArc(sketch, "E215", {"start": v(68.5, -84.87) * mm, "mid": v(70.04, -90.62) * mm, "end": v(74.25, -94.83) * mm, "construction": true});
            skArc(sketch, "E216.trimOffspring", {"start": v(91.5, -84.87) * mm, "mid": v(89.96, -79.12) * mm, "end": v(85.75, -74.91) * mm, "construction": true});
            skArc(sketch, "E217.0.startCap", {"start": v(67.5, -84.87) * mm, "mid": v(68.5, -83.87) * mm, "end": v(69.5, -84.87) * mm});
            skArc(sketch, "E217.0.endCap", {"start": v(74.75, -93.96) * mm, "mid": v(75.12, -95.33) * mm, "end": v(73.75, -95.7) * mm});
            skArc(sketch, "E217.0.left", {"start": v(69.5, -84.87) * mm, "mid": v(70.9, -90.12) * mm, "end": v(74.75, -93.96) * mm});
            skArc(sketch, "E217.0.right", {"start": v(67.5, -84.87) * mm, "mid": v(69.17, -91.12) * mm, "end": v(73.75, -95.7) * mm});
            skArc(sketch, "E217.1.startCap", {"start": v(92.5, -84.87) * mm, "mid": v(91.5, -85.87) * mm, "end": v(90.5, -84.87) * mm});
            skArc(sketch, "E217.1.endCap", {"start": v(85.25, -75.78) * mm, "mid": v(84.88, -74.41) * mm, "end": v(86.25, -74.05) * mm});
            skArc(sketch, "E217.1.left", {"start": v(90.5, -84.87) * mm, "mid": v(89.1, -79.62) * mm, "end": v(85.25, -75.78) * mm});
            skArc(sketch, "E217.1.right", {"start": v(92.5, -84.87) * mm, "mid": v(90.83, -78.62) * mm, "end": v(86.25, -74.05) * mm});
            skPoint(sketch, "E218.visualSharp", {"position": v(-54.3, -76.9) * mm});
            skPoint(sketch, "E219.visualSharp", {"position": v(76, -77.94) * mm});
            skArc(sketch, "E220.MirrorCS", {"start": v(92.5, 84.87) * mm, "mid": v(91.5, 85.87) * mm, "end": v(90.5, 84.87) * mm});
            skArc(sketch, "E221.MirrorCS", {"start": v(85.25, 75.78) * mm, "mid": v(84.88, 74.41) * mm, "end": v(86.25, 74.05) * mm});
            skArc(sketch, "E222.MirrorCS", {"start": v(92.5, 84.87) * mm, "mid": v(90.83, 78.62) * mm, "end": v(86.25, 74.05) * mm});
            skArc(sketch, "E223.MirrorCS", {"start": v(90.5, 84.87) * mm, "mid": v(89.1, 79.62) * mm, "end": v(85.25, 75.78) * mm});
            skArc(sketch, "E224.MirrorCS", {"start": v(67.5, 84.87) * mm, "mid": v(68.5, 83.87) * mm, "end": v(69.5, 84.87) * mm});
            skArc(sketch, "E225.MirrorCS", {"start": v(74.75, 93.96) * mm, "mid": v(75.12, 95.33) * mm, "end": v(73.75, 95.7) * mm});
            skArc(sketch, "E226.MirrorCS", {"start": v(69.5, 84.87) * mm, "mid": v(70.9, 90.12) * mm, "end": v(74.75, 93.96) * mm});
            skArc(sketch, "E227.MirrorCS", {"start": v(67.5, 84.87) * mm, "mid": v(69.17, 91.12) * mm, "end": v(73.75, 95.7) * mm});
            skArc(sketch, "E228.MirrorCS", {"start": v(-44.76, 92.04) * mm, "mid": v(-46.15, 92.29) * mm, "end": v(-46.4, 90.9) * mm});
            skArc(sketch, "E229.MirrorCS", {"start": v(-44.76, 92.04) * mm, "mid": v(-42.55, 85.96) * mm, "end": v(-43.67, 79.59) * mm});
            skArc(sketch, "E230.MirrorCS", {"start": v(-45.48, 80.43) * mm, "mid": v(-45, 79.1) * mm, "end": v(-43.67, 79.59) * mm});
            skArc(sketch, "E231.MirrorCS", {"start": v(-46.4, 90.9) * mm, "mid": v(-44.54, 85.79) * mm, "end": v(-45.48, 80.43) * mm});
            skArc(sketch, "E232.MirrorCS", {"start": v(-64.52, 89.3) * mm, "mid": v(-65, 90.64) * mm, "end": v(-66.33, 90.15) * mm});
            skArc(sketch, "E233.MirrorCS", {"start": v(-65.24, 77.7) * mm, "mid": v(-63.85, 77.46) * mm, "end": v(-63.6, 78.85) * mm});
            skArc(sketch, "E234.MirrorCS", {"start": v(-65.24, 77.7) * mm, "mid": v(-67.45, 83.78) * mm, "end": v(-66.33, 90.15) * mm});
            skArc(sketch, "E235.MirrorCS", {"start": v(-63.6, 78.85) * mm, "mid": v(-65.46, 83.96) * mm, "end": v(-64.52, 89.3) * mm});
            skCircle(sketch, "E236", {"center": v(-27.5, -12) * mm, "radius": 1.5 * mm});
            skCircle(sketch, "E237.MirrorC", {"center": v(-27.5, 12) * mm, "radius": 1.5 * mm});
            skSolve(sketch);
        }
        {
            var Q0;
            Q0=makeQuery(id+"F0.imprint","IMPRINT",FACE,{"disambiguationData":[TD([[makeQuery(id+"F0.imprint","IMPRINT",EDGE,{"derivedFrom":sQuery(id+"F0.wireOp",EDGE,"E3")}),1.0]])]});
            extrude(context, id + "F1", {"entities" : qUnion([Q0]), "depth" : 2 * mm});
        }
    });
